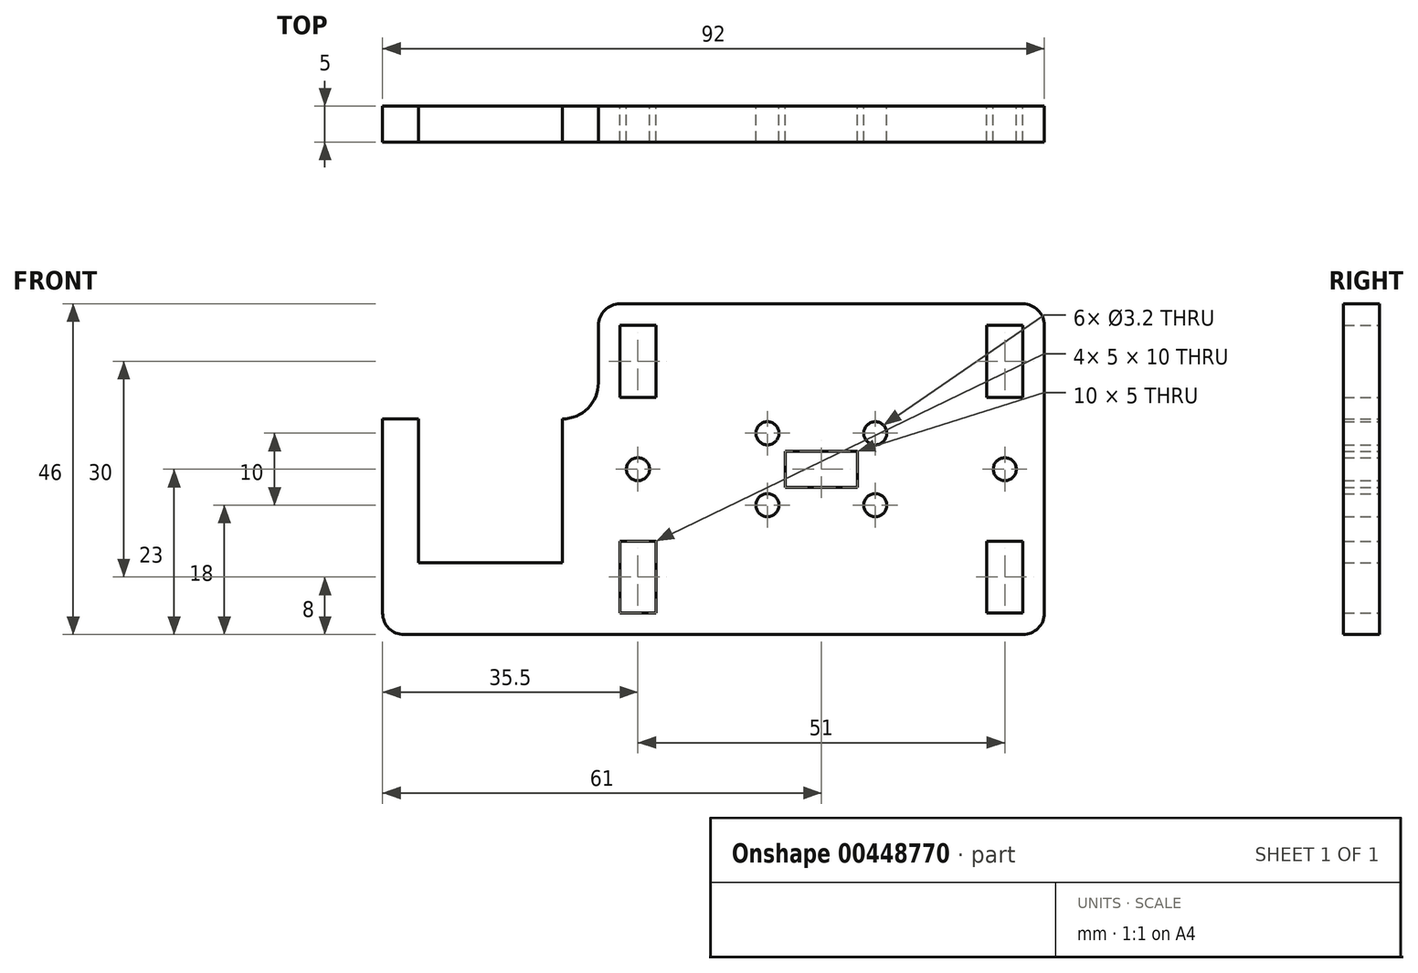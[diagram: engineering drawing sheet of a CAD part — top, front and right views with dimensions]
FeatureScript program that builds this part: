
annotation { "Feature Type Name" : "Feature", "Feature Type Description" : "" }
export const myFeature = defineFeature(function(context is Context, id is Id, definition is map)
    precondition{}
    {
        {
            assignVariable(context, id + "F0", {"name" : "thickness", "anyValue" : 5 * mm});
        }
        {
            var Q0;
            Q0=qCreatedBy(makeId("Front.planeOp"),FACE);
            var sketch = newSketch(context, id + "F1", { "sketchPlane" : qUnion([Q0])});
            skLineSegment(sketch, "E0.bottom", {"start": v(0, 0) * mm, "end": v(20, 0) * mm, "construction": true});
            skLineSegment(sketch, "E0.top", {"start": v(0, 30) * mm, "end": v(20, 30) * mm, "construction": true});
            skLineSegment(sketch, "E0.left", {"start": v(0, 0) * mm, "end": v(0, 30) * mm, "construction": true});
            skLineSegment(sketch, "E0.right", {"start": v(20, 0) * mm, "end": v(20, 30) * mm, "construction": true});
            skLineSegment(sketch, "E1.bottom", {"start": v(2.5, 20) * mm, "end": v(17.5, 20) * mm, "construction": true});
            skLineSegment(sketch, "E1.top", {"start": v(2.5, 10) * mm, "end": v(17.5, 10) * mm, "construction": true});
            skLineSegment(sketch, "E1.left", {"start": v(2.5, 20) * mm, "end": v(2.5, 10) * mm, "construction": true});
            skLineSegment(sketch, "E1.right", {"start": v(17.5, 20) * mm, "end": v(17.5, 10) * mm, "construction": true});
            skPoint(sketch, "E2", {"position": v(10, 30) * mm});
            skPoint(sketch, "E3", {"position": v(10, 20) * mm});
            skPoint(sketch, "E4", {"position": v(2.5, 15) * mm});
            skPoint(sketch, "E5", {"position": v(0, 15) * mm});
            skCircle(sketch, "E6", {"center": v(2.5, 20) * mm, "radius": 1.6 * mm});
            skCircle(sketch, "E7", {"center": v(17.5, 20) * mm, "radius": 1.6 * mm});
            skCircle(sketch, "E8", {"center": v(17.5, 10) * mm, "radius": 1.6 * mm});
            skCircle(sketch, "E9", {"center": v(2.5, 10) * mm, "radius": 1.6 * mm});
            skLineSegment(sketch, "E10.0", {"start": v(-21, 27) * mm, "end": v(-21, 35) * mm});
            skLineSegment(sketch, "E10.2", {"start": v(41, -5) * mm, "end": v(41, 35) * mm});
            skLineSegment(sketch, "E11.bottom", {"start": v(-18, 35) * mm, "end": v(-13, 35) * mm});
            skLineSegment(sketch, "E11.top", {"start": v(-18, 25) * mm, "end": v(-13, 25) * mm});
            skLineSegment(sketch, "E11.left", {"start": v(-18, 35) * mm, "end": v(-18, 25) * mm});
            skLineSegment(sketch, "E11.right", {"start": v(-13, 35) * mm, "end": v(-13, 25) * mm});
            skLineSegment(sketch, "E12", {"start": v(-21, 15) * mm, "end": v(41, 15) * mm, "construction": true});
            skLineSegment(sketch, "E13.MirrorCS", {"start": v(-18, -5) * mm, "end": v(-18, 5) * mm});
            skLineSegment(sketch, "E14.MirrorCS", {"start": v(-18, -5) * mm, "end": v(-13, -5) * mm});
            skLineSegment(sketch, "E15.MirrorCS", {"start": v(-13, -5) * mm, "end": v(-13, 5) * mm});
            skLineSegment(sketch, "E16.MirrorCS", {"start": v(-18, 5) * mm, "end": v(-13, 5) * mm});
            skLineSegment(sketch, "E17", {"start": v(10, 38) * mm, "end": v(10, -8) * mm, "construction": true});
            skLineSegment(sketch, "E18.MirrorCS", {"start": v(38, 35) * mm, "end": v(33, 35) * mm});
            skLineSegment(sketch, "E19.MirrorCS", {"start": v(38, 35) * mm, "end": v(38, 25) * mm});
            skLineSegment(sketch, "E20.MirrorCS", {"start": v(33, 35) * mm, "end": v(33, 25) * mm});
            skLineSegment(sketch, "E21.MirrorCS", {"start": v(38, 25) * mm, "end": v(33, 25) * mm});
            skLineSegment(sketch, "E22.MirrorCS", {"start": v(38, -5) * mm, "end": v(38, 5) * mm});
            skLineSegment(sketch, "E23.MirrorCS", {"start": v(38, 5) * mm, "end": v(33, 5) * mm});
            skLineSegment(sketch, "E24.MirrorCS", {"start": v(33, -5) * mm, "end": v(33, 5) * mm});
            skLineSegment(sketch, "E25.MirrorCS", {"start": v(38, -5) * mm, "end": v(33, -5) * mm});
            skCircle(sketch, "E26", {"center": v(-15.5, 15) * mm, "radius": 1.6 * mm});
            skPoint(sketch, "E27", {"position": v(-15.5, 25) * mm});
            skCircle(sketch, "E28.MirrorC", {"center": v(35.5, 15) * mm, "radius": 1.6 * mm});
            skLineSegment(sketch, "E29.bottom", {"start": v(5, 17.5) * mm, "end": v(15, 17.5) * mm});
            skLineSegment(sketch, "E29.top", {"start": v(5, 12.5) * mm, "end": v(15, 12.5) * mm});
            skLineSegment(sketch, "E29.left", {"start": v(5, 17.5) * mm, "end": v(5, 12.5) * mm});
            skLineSegment(sketch, "E29.right", {"start": v(15, 17.5) * mm, "end": v(15, 12.5) * mm});
            skPoint(sketch, "E30", {"position": v(5, 15) * mm});
            skPoint(sketch, "E31", {"position": v(10, 17.5) * mm});
            skLineSegment(sketch, "E32", {"start": v(-18, 38) * mm, "end": v(38, 38) * mm});
            skLineSegment(sketch, "E33", {"start": v(-48, -8) * mm, "end": v(38, -8) * mm});
            skPoint(sketch, "E34.visualSharp", {"position": v(-21, 38) * mm});
            skArc(sketch, "E34.filletArc", {"start": v(-18, 38) * mm, "mid": v(-20.12, 37.12) * mm, "end": v(-21, 35) * mm});
            skPoint(sketch, "E35.visualSharp", {"position": v(41, 38) * mm});
            skArc(sketch, "E35.filletArc", {"start": v(41, 35) * mm, "mid": v(40.12, 37.12) * mm, "end": v(38, 38) * mm});
            skPoint(sketch, "E36.visualSharp", {"position": v(-21, -8) * mm});
            skPoint(sketch, "E37.visualSharp", {"position": v(41, -8) * mm});
            skArc(sketch, "E37.filletArc", {"start": v(38, -8) * mm, "mid": v(40.12, -7.12) * mm, "end": v(41, -5) * mm});
            skLineSegment(sketch, "E38", {"start": v(-51, 22) * mm, "end": v(-51, -5) * mm});
            skLineSegment(sketch, "E39.0", {"start": v(-46, 2) * mm, "end": v(-26, 2) * mm});
            skLineSegment(sketch, "E40", {"start": v(-26, 22) * mm, "end": v(-26, 2) * mm});
            skPoint(sketch, "E41.visualSharp", {"position": v(-51, -8) * mm});
            skArc(sketch, "E41.filletArc", {"start": v(-51, -5) * mm, "mid": v(-50.12, -7.12) * mm, "end": v(-48, -8) * mm});
            skPoint(sketch, "E42.visualSharp", {"position": v(-21, 22) * mm});
            skArc(sketch, "E42.filletArc", {"start": v(-26, 22) * mm, "mid": v(-22.46, 23.46) * mm, "end": v(-21, 27) * mm});
            skLineSegment(sketch, "E43", {"start": v(-46, 2) * mm, "end": v(-46, 22) * mm});
            skLineSegment(sketch, "E44", {"start": v(-46, 22) * mm, "end": v(-51, 22) * mm});
            skSolve(sketch);
        }
        {
            var Q0;
            Q0=qSketchRegion(id+"F1",true);
            extrude(context, id + "F2", {"entities" : qUnion([Q0]), "depth" : getVariable(context, 'thickness')});
        }
    });
